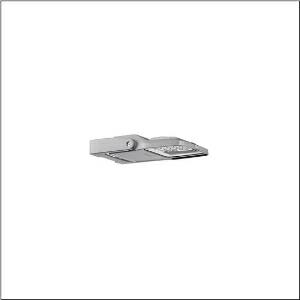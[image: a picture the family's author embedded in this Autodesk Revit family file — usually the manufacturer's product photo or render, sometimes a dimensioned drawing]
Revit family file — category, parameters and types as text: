
# Revit family: floodlight_fl_21_micro___pl64_5xa7762a2e2a_6a16
name_source: partatom
category: Lighting Fixtures
units: mm (PartAtom-declared; Revit-internal decimal feet)

## family parameters
Cut with Voids When Loaded = No
Host = Face
Light Source = No
Part Type = Normal
Room Calculation Point = No
Round Connector Dimension = Use Diameter
Shared = No

## types (1)
- --- (1 x LED, 2870 lm, 23.1 W, 3000K)
    Apparent Load = 23 VA
    CIE Flux Codes = 28 80 98 100 100
    Color Rendering = 70
    Color Temperature = 3000K
    Default Elevation = 1800 mm
    Description = Floodlight FL 21 micro, floodlight, primary light control with lens, of PMMA, primary optical cover: protective disc, of toughened safety glass, transparent, light distribution: PL64, light emission: direct distribution, installation type: surface-mounted, LED, High Power LED, rated luminous flux: 2.870lm, luminous efficacy: 124lm/W, light colour: 730, colour temperature: 3000K, control gear: ECG iQ, control: Auto-Match, Temp-Guard, Night-Set, Smart-Wire, Desk-Remote (wireless, voltage-free reading and setting of iQ features in the workshop via application-optimized NFC function/RFID function), optimised constant luminous flux control (CLO 2.0), Street-Remote, with terminal, 6-pole, mains connection: 220..240V, AC, 50/60Hz, start of lifetime: 23W, end of lifetime: 24W, reduction: 11W, luminaire housing, of diecast aluminium, powder-coated, Siteco® metallic grey (DB 702S), corrosivity category C5 according to DIN EN ISO 12944, design bracket, of diecast aluminium, powder-coated, Siteco® metallic grey (DB 702S), protection rating (complete): IP66, insulation class (complete): insulation class II (safety insulation), certification: CE, protection symbol: D, impact resistance: IK07, permissible operating ambient temperature: -40..+40°C, permissible operating ambient temperature for outdoor applications: -40..+50°C, standard: DIN EN 12944, packaging unit: 1 piece

Light Distribution: PL64
    Height = 65 mm
    Lamp = 1 x LED
    Lamp Light Flux = 2870 lm
    Lamp Power = 23.1 W
    Lamp count = 1
    Length = 312 mm
    Luminous efficacy = 124 lm/W
    Manufacturer = Siteco
    ModVariant = No
    Model = 5XA7762A2E2A
    Number of Poles = 1
    OnlyDefault = Yes
    Power Factor = 1
    Product Name = Floodlight FL 21 micro | PL64
    Product group = floodlight | pylon top
    ProductGroupID = 6101
    Protection Class = Protection class II
    Protection Degree = IP 66
    RLX_Detail_Level = 1
    RlxData = <blob elided: 97129 chars, md5=ed54b9a9>
    Socket = socket
    Standby Power = 0 W
    System Light Flux = 2870 lm
    System Power = 23 W
    Type Comments = factory setting: luminous flux: 100 % | dim-lin: 254 | 455 mA
    Type Image = l_1006878.jpg
    URL = http://relux.com
    VarID = @adj_094203
    Voltage = 0 V
    Weight = 0.00 kg
    Width = 230 mm

## geometry (parser evidence)
native form markers: Blend x4, Sweep x12
no freeform markers — native parametric forms only
